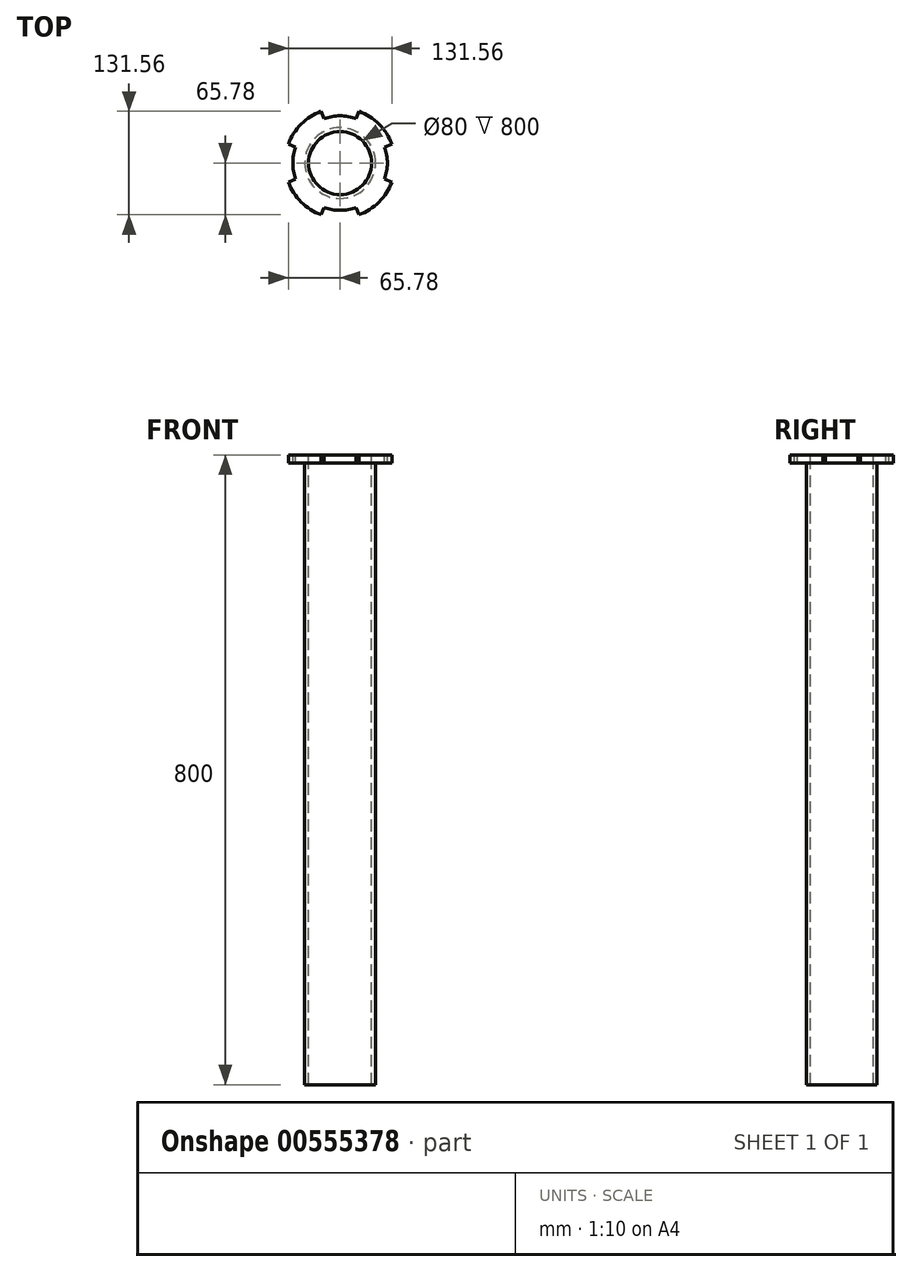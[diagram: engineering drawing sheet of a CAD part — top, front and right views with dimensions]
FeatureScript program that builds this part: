
annotation { "Feature Type Name" : "Feature", "Feature Type Description" : "" }
export const myFeature = defineFeature(function(context is Context, id is Id, definition is map)
    precondition{}
    {
        {
            var Q0;
            Q0=qCreatedBy(makeId("Top.planeOp"),FACE);
            var sketch = newSketch(context, id + "F0", { "sketchPlane" : qUnion([Q0])});
            skCircle(sketch, "E0", {"center": v(0, 0) * mm, "radius": 45 * mm});
            skCircle(sketch, "E1.0", {"center": v(0, 0) * mm, "radius": 40 * mm});
            skSolve(sketch);
        }
        {
            var Q0;
            Q0 = qSketchRegion(id + "F0", true);
            extrude(context, id + "F1", {"entities" : qUnion([Q0]), "oppositeDirection" : true, "depth" : 800 * mm, "offsetDistance" : 25 * mm});
        }
        {
            var Q0;
            Q0=qCreatedBy(makeId("Top.planeOp"),FACE);
            var sketch = newSketch(context, id + "F2", { "sketchPlane" : qUnion([Q0])});
            skCircle(sketch, "E2.0", {"center": v(0, 0) * mm, "radius": 45 * mm});
            skCircle(sketch, "E3.0", {"center": v(0, 0) * mm, "radius": 70 * mm});
            skSolve(sketch);
        }
        {
            var Q0;
            Q0 = qSketchRegion(id + "F2", true);
            extrude(context, id + "F3", {"entities" : qUnion([Q0]), "operationType" : NewBodyOperationType.ADD, "oppositeDirection" : true, "depth" : 10 * mm, "offsetDistance" : 25 * mm});
        }
        {
            var Q0;
            Q0=qCreatedBy(makeId("Top.planeOp"),FACE);
            var sketch = newSketch(context, id + "F4", { "sketchPlane" : qUnion([Q0])});
            skArc(sketch, "E4.0", {"start": v(65.78, -23.94) * mm, "mid": v(70, 0) * mm, "end": v(65.78, 23.94) * mm});
            skArc(sketch, "E5.0", {"start": v(56.38, -20.52) * mm, "mid": v(60, 0) * mm, "end": v(56.38, 20.52) * mm});
            skLineSegment(sketch, "E6", {"start": v(60, 0) * mm, "end": v(70, 0) * mm});
            skLineSegment(sketch, "E7.1.0", {"start": v(56.38, -20.52) * mm, "end": v(65.78, -23.94) * mm});
            skLineSegment(sketch, "E7.anchor1", {"start": v(0, 0) * mm, "end": v(60, 0) * mm, "construction": true});
            skLineSegment(sketch, "E7.anchor2", {"start": v(0, 0) * mm, "end": v(56.38, -20.52) * mm, "construction": true});
            skLineSegment(sketch, "E8.MirrorCS", {"start": v(56.38, 20.52) * mm, "end": v(65.78, 23.94) * mm});
            skSolve(sketch);
        }
        {
            var Q0;
            Q0 = qSketchRegion(id + "F4", true);
            extrude(context, id + "F5", {"entities" : qUnion([Q0]), "endBound" : BoundingType.UP_TO_NEXT, "oppositeDirection" : true, "depth" : 25 * mm, "offsetDistance" : 25 * mm});
        }
        {
            var Q0;
            Q0=makeQuery(id+"F5.opExtrude","SWEPT_BODY",BODY,{"disambiguationData":[OSD([sQuery(id+"F4.wireOp",EDGE,"E4.0"),sQuery(id+"F4.wireOp",EDGE,"E5.0"),sQuery(id+"F4.wireOp",EDGE,"E7.1.0"),sQuery(id+"F4.wireOp",EDGE,"E8.MirrorCS")])]});
            var Q1;
            Q1=makeQuery(id+"F1.opExtrude","SWEPT_FACE",FACE,{"disambiguationData":[OSD([sQuery(id+"F0.wireOp",EDGE,"E0")])]});
            circularPattern(context, id + "F6", {"operationType" : NewBodyOperationType.REMOVE, "entities" : qUnion([Q0]), "axis" : qUnion([Q1]), "angle" : 360 * degree, "instanceCount" : 4, "equalSpace" : true});
        }
    });
